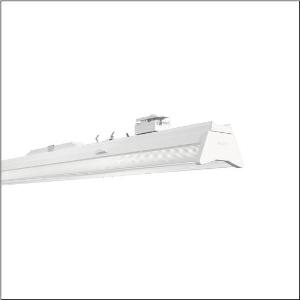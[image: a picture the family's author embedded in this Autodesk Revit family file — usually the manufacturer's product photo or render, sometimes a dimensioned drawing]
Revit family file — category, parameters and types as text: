
# Revit family: licross_r__21_performance_mo_52tm16dn4a5g_341e
name_source: partatom
category: Lighting Fixtures
units: mm (PartAtom-declared; Revit-internal decimal feet)

## family parameters
Cut with Voids When Loaded = No
Host = Face
Light Source = No
Part Type = Normal
Room Calculation Point = No
Round Connector Dimension = Use Diameter
Shared = No

## types (1)
- --- (1 x LED, 10840 lm, 62 W, 4000K)
    Apparent Load = 62 VA
    CIE Flux Codes = 66 88 96 79 100
    Color Rendering = 80
    Color Temperature = 4000K
    Default Elevation = 1800 mm
    Description = Licross® 21 Performance MO, luminaire insert, of sheet steel, galvanised, coil coated, white, length: 1.500mm, width: 120mm, height: 123mm, LED rated luminous flux: 10.840lm, light colour: 840, control gear: DALI 2, with plug, 5-pole, with phase selection, mains connection: 220..240V, AC, 50/60Hz, rated input power: 62W, halogen-free wiring, primary light control with lens, of plastic, primary optical cover: cover, of PMMA, light emission: direct/indirect distribution, primary light characteristic: symmetric, protection rating (complete): IP40, insulation class (complete): insulation class I (protective earthing), certification: CE, ENEC, UKCA, protection symbol: D if used in an environment without relevant dust loads with corresponding accessories, impact resistance: IK06, permissible ambient temperature for indoor applications: -25..+35°C, corresponds to IFS (International Featured Standards) requirements for safety and quality in the food industry, reducing of maximum allowable ambient temperature of 5°C with ceiling mounting, LABS conformity tested according to VDMA 24364:2018-05, packaging unit: 1 piece
    Height = 114 mm
    Lamp = 1 x LED
    Lamp Light Flux = 10840 lm
    Lamp Power = 62 W
    Lamp count = 1
    Length = 1500 mm
    Luminous efficacy = 175 lm/W
    Manufacturer = Siteco
    ModVariant = No
    Model = 52TM16DN4A5G
    Mounting Place = Ceiling
    Mounting Type = Pendant
    Number of Poles = 1
    OnlyDefault = Yes
    Power Factor = 1
    Product Name = Licross® 21 Performance MO
    Product group = luminaire insert
    ProductGroupID = 901
    Protection Class = Protection class I
    Protection Degree = IP 40
    RLX_Detail_Level = 1
    RLX_Emergency_Light_Flux = 0 lm
    RLX_Emergency_Type = 0
    RLX_Emergency_Type_DB = No
    RlxData = <blob elided: 33977 chars, md5=b64b9423>
    Socket = socket
    Standby Power = 0 W
    System Light Flux = 10840 lm
    System Power = 62 W
    Type Comments = factory setting: luminous flux: 100 % | dim-lin: 254 | 418 mA
    Type Image = l_1256138.jpg
    URL = http://relux.com
    VarID = @adj_060837
    Voltage = 0 V
    Weight = 0.00 kg
    Width = 120 mm

## geometry (parser evidence)
native form markers: Blend x4, Sweep x13
no freeform markers — native parametric forms only
